# Revit family: Haworth_HATElements_BenchSingle_120Deg_AP_PRELIMINARY
name_source: partatom
category: Furniture Systems
units: mm (PartAtom-declared; Revit-internal decimal feet)

## family parameters
Always vertical = Yes
Cut with Voids When Loaded = No
OmniClass Number = 23.40.70.14.64.21
OmniClass Title = Systems Furniture
Part Type = Normal
Room Calculation Point = No
Round Connector Dimension = Use Diameter
Shared = No
Work Plane-Based = No

## types (4) — shared parameters
Actual Height = 730 mm  [stored 2.39501 ft]
Actual Width = 1200 mm
Assembly Code = E2020200
Base Tube Finish = Haworth _ Paint _ Smoke
Box Body Finish = Haworth _ Paint _ Black
Cable Tray Finish = Haworth _ Polymer _ Undecided
Description = Haworth - HAT Elements - Single Bench - 120 Degree
Flip Top Finish = Haworth _ Paint _ Metallic Silver
Leg Height = 695 mm  [stored 2.28018 ft]
Leg Side Offset = 50 mm  [stored 0.164042 ft]
Manufacturer = Haworth
Model = SYEL12S12XX
Revision Number = 1
Size = Verify Final Dim. w/ Haworth
Table Thickness = 35 mm  [stored 0.114829 ft]
Trim Finish = Haworth _ Paint _ Black
URL = https://www.haworth.com
URL - Product = https://www.haworth.com
Warranty = http://www.haworth.com
Worksurface Depth = 600, 700, 750, 800 mm
Worksurface Width = 1200 mm
with Worktop = Yes

## per-type parameters (varying)
| type | Actual Depth | Cable Tray | Flip Top | Leg Back Offset | Round Leg | Round Motorized | Square Leg | Square Motorized | Umbilical Cord to Floor | Umbilical Cord to Trunk | with Cable Trunk | without Umbilical Cord |
| 1200 x 600 | 600 mm | No | No | 165 mm | No | No | Yes | Yes | No | No | No | Yes |
| 1200 x 700 | 700 mm  [stored 2.29659 ft] | Yes | Yes | 165 mm | Yes | Yes | No | No | No | Yes | Yes | No |
| 1200 x 750 | 750 mm  [stored 2.46063 ft] | Yes | Yes | 231 mm | No | No | Yes | Yes | Yes | No | No | No |
| 1200 x 800 | 800 mm  [stored 2.62467 ft] | Yes | Yes | 231 mm | Yes | Yes | No | Yes | No | Yes | Yes | No |

type visibility flags: 4 boolean params named "<type name>" — each type sets only its own to Yes (folded from table)

note: [stored X ft] marks values corroborated as IEEE doubles in the binary element streams (Revit-internal decimal feet)

## geometry (parser evidence)
native form markers: Sweep x26
no freeform markers — native parametric forms only
